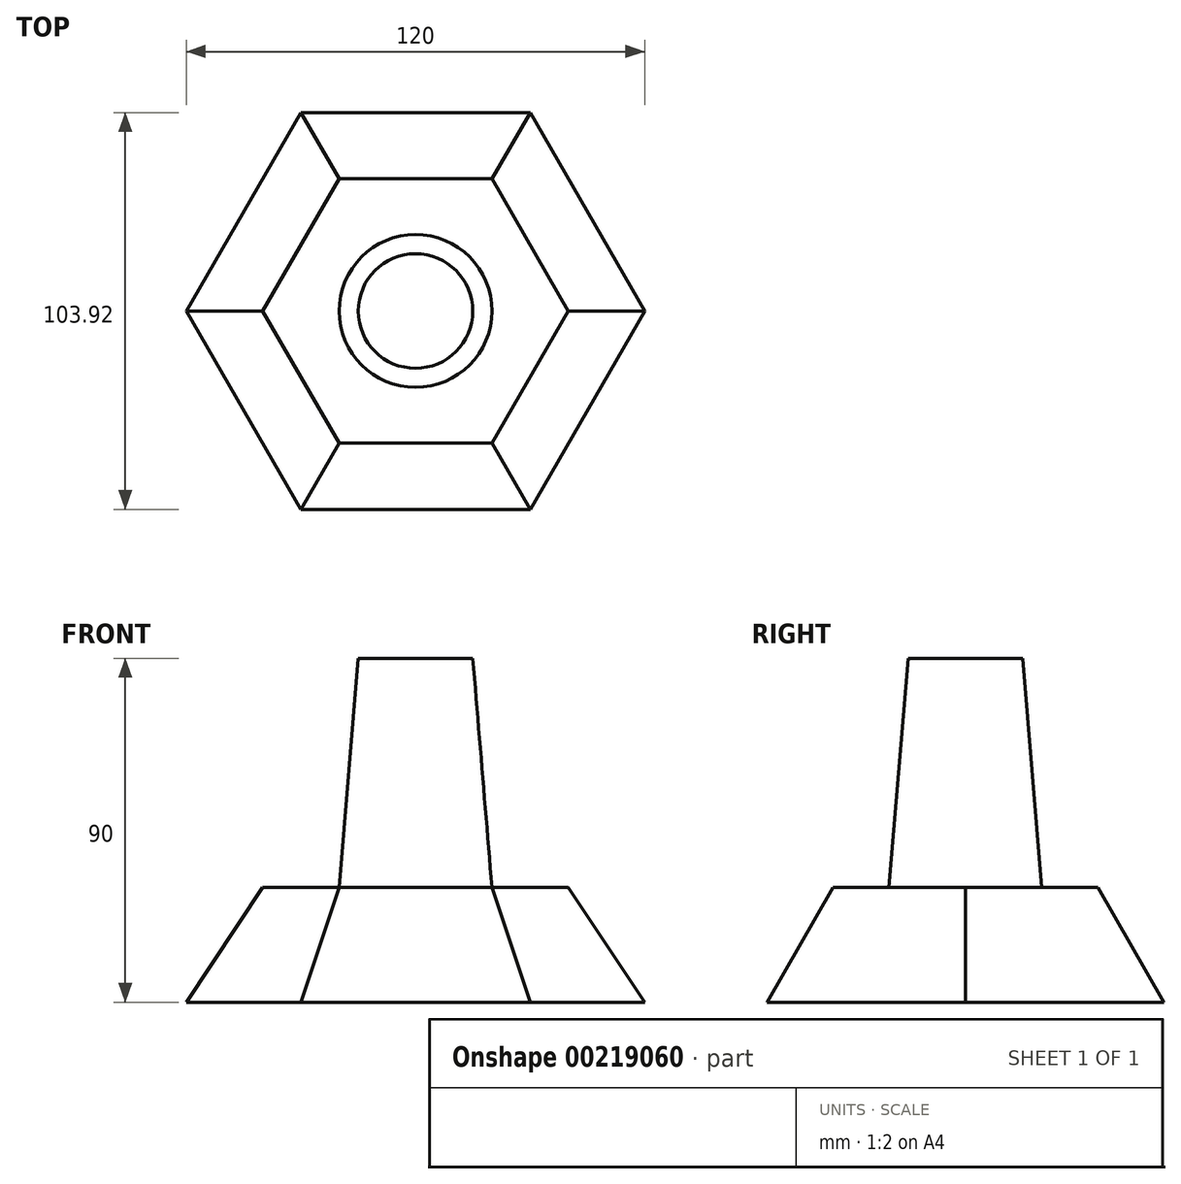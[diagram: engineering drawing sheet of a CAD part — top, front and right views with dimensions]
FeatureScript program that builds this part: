
annotation { "Feature Type Name" : "Feature", "Feature Type Description" : "" }
export const myFeature = defineFeature(function(context is Context, id is Id, definition is map)
    precondition{}
    {
        {
            var Q0;
            Q0=qCreatedBy(makeId("Top.planeOp"),FACE);
            var sketch = newSketch(context, id + "F0", { "sketchPlane" : qUnion([Q0])});
            skCircle(sketch, "E0.cCircle", {"center": v(0, 0) * mm, "radius": 51.96 * mm, "construction": true});
            skLineSegment(sketch, "E0.0", {"start": v(30, 51.96) * mm, "end": v(60, 0) * mm});
            skLineSegment(sketch, "E0.1", {"start": v(60, 0) * mm, "end": v(30, -51.96) * mm});
            skLineSegment(sketch, "E0.2", {"start": v(30, -51.96) * mm, "end": v(-30, -51.96) * mm});
            skLineSegment(sketch, "E0.3", {"start": v(-30, -51.96) * mm, "end": v(-60, 0) * mm});
            skLineSegment(sketch, "E0.4", {"start": v(-60, 0) * mm, "end": v(-30, 51.96) * mm});
            skLineSegment(sketch, "E0.5", {"start": v(-30, 51.96) * mm, "end": v(30, 51.96) * mm});
            skPoint(sketch, "E0.0.midPoint", {"position": v(45, 25.98) * mm});
            skSolve(sketch);
        }
        {
            var Q0;
            Q0=qCreatedBy(makeId("Top.planeOp"),FACE);
            cPlane(context, id + "F1", {"entities" : qUnion([Q0]), "cplaneType" : CPlaneType.OFFSET, "offset" : 30 * mm, "width" : 150 * mm, "height" : 150 * mm});
        }
        {
            var Q0;
            Q0=qCreatedBy(id+"F1.planeOp",FACE);
            var sketch = newSketch(context, id + "F2", { "sketchPlane" : qUnion([Q0])});
            skCircle(sketch, "E1.cCircle", {"center": v(0, 0) * mm, "radius": 34.64 * mm, "construction": true});
            skLineSegment(sketch, "E1.0", {"start": v(20, 34.64) * mm, "end": v(40, 0) * mm});
            skLineSegment(sketch, "E1.1", {"start": v(40, 0) * mm, "end": v(20, -34.64) * mm});
            skLineSegment(sketch, "E1.2", {"start": v(20, -34.64) * mm, "end": v(-20, -34.64) * mm});
            skLineSegment(sketch, "E1.3", {"start": v(-20, -34.64) * mm, "end": v(-40, 0) * mm});
            skLineSegment(sketch, "E1.4", {"start": v(-40, 0) * mm, "end": v(-20, 34.64) * mm});
            skLineSegment(sketch, "E1.5", {"start": v(-20, 34.64) * mm, "end": v(20, 34.64) * mm});
            skPoint(sketch, "E1.0.midPoint", {"position": v(30, 17.32) * mm});
            skSolve(sketch);
        }
        {
            var Q0;
            Q0=qCreatedBy(id+"F1.planeOp",FACE);
            cPlane(context, id + "F3", {"entities" : qUnion([Q0]), "cplaneType" : CPlaneType.OFFSET, "offset" : 60 * mm, "width" : 150 * mm, "height" : 150 * mm});
        }
        {
            var Q0;
            Q0=qCreatedBy(id+"F3.planeOp",FACE);
            var sketch = newSketch(context, id + "F4", { "sketchPlane" : qUnion([Q0])});
            skCircle(sketch, "E2", {"center": v(0, 0) * mm, "radius": 15 * mm});
            skSolve(sketch);
        }
        {
            var Q0;
            Q0=makeQuery(id+"F2.imprint","IMPRINT",FACE,{"disambiguationData":[TD([[makeQuery(id+"F2.imprint","IMPRINT",EDGE,{"derivedFrom":sQuery(id+"F2.wireOp",EDGE,"E1.0")}),-1.0]])]});
            var sketch = newSketch(context, id + "F5", { "sketchPlane" : qUnion([Q0])});
            skCircle(sketch, "E3", {"center": v(0, 0) * mm, "radius": 20 * mm});
            skSolve(sketch);
        }
        {
            var Q0;
            Q0=makeQuery(id+"F0.imprint","IMPRINT",FACE,{"disambiguationData":[TD([[makeQuery(id+"F0.imprint","IMPRINT",EDGE,{"derivedFrom":sQuery(id+"F0.wireOp",EDGE,"E0.0")}),-1.0]])]});
            var Q1;
            Q1 = qSketchRegion(id + "F2", true);
            loft(context, id + "F6", {"sheetProfilesArray" : [{ "sheetProfileEntities" : qUnion([Q0]) }, { "sheetProfileEntities" : qUnion([Q1]) }]});
        }
        {
            var Q1;
            Q1 = qSketchRegion(id + "F5", true);
            var Q2;
            Q2 = qSketchRegion(id + "F4", true);
            loft(context, id + "F7", {"operationType" : NewBodyOperationType.ADD, "sheetProfilesArray" : [{ "sheetProfileEntities" : qUnion([Q1]) }, { "sheetProfileEntities" : qUnion([Q2]) }]});
        }
    });
